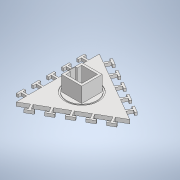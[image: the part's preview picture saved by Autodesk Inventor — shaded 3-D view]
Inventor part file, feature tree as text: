
AUTODESK INVENTOR PART (.ipt)
format: ipt  version: 2022.3 (Build 263350000, 350)  size: 408,576 bytes
history: native  units: mm
features: extrude x6, sketch x5
ambient origin geometry x8: Origin, YZ Plane, XZ Plane, XY Plane, X Axis, Y Axis, Z Axis, Center Point
bodies: Solid1 (feature_tree)
feature tree (11):
  sketch  "Sketch1"  dims[d1=220.0mm d2=35.0mm]
  extrude  "Extrusion1"  Depth=35.0mm
  extrude  "Extrusion2"  Depth=5.0mm
  sketch  "Sketch2"  dims[d3=5.0mm d4=5.0mm]
  extrude  "Extrusion3"  Depth=30.0mm
  extrude  "Extrusion4"  Depth=30.0mm
  extrude  "Extrusion5"  Depth=10.0mm TaperAngle=0.0deg
  extrude  "Extrusion6"  Depth=2.5mm TaperAngle=0.0deg
  sketch  "Sketch3"  dims[d5=20.0mm d6=30.0mm d8=40.0mm d9=30.0mm d11=40.0mm]
  sketch  "Sketch4"  dims[d14=30.0mm d16=240.0deg d18=30.0mm d20=40.0mm d21=30.0mm d23=40.0mm]
  sketch  "Sketch5"  dims[d26=30.0mm d28=40.0mm d29=30.0mm d31=40.0mm d34=10.0mm d35=0.0mm d36=2.5mm d37=0.0mm d38=42.0mm d39=42.0mm d40=6.0mm d41=20.0mm d42=10.0mm d43=18.0mm d44=40.0mm d45=0.0mm d46=5.0mm d47=3.0mm d48=0.0mm d49=10.0mm d50=3.0mm d51=0.0mm d52=80.0mm d53=4.0mm d54=2.0mm d55=0.0mm]
